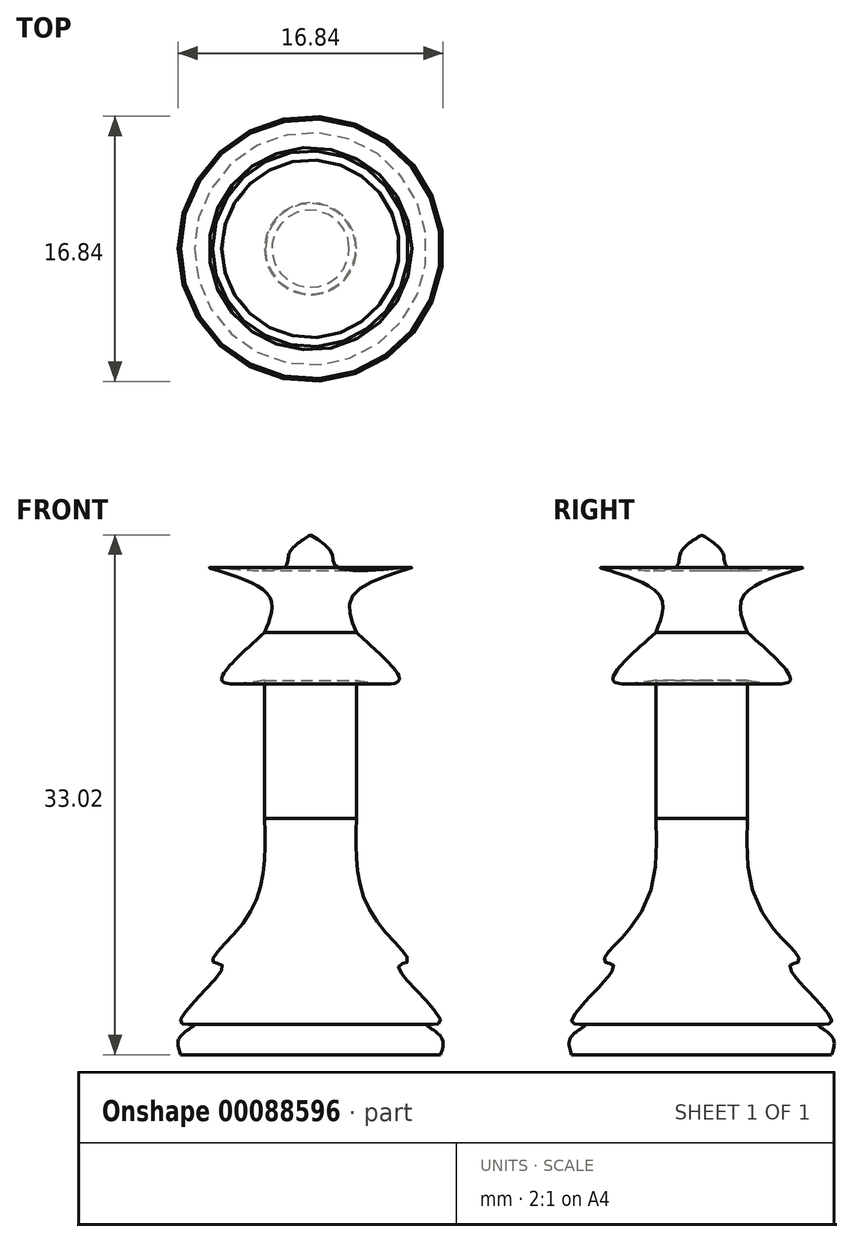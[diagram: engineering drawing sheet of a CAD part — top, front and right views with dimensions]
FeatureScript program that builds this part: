
annotation { "Feature Type Name" : "Feature", "Feature Type Description" : "" }
export const myFeature = defineFeature(function(context is Context, id is Id, definition is map)
    precondition{}
    {
        {
            var Q0;
            Q0=qCreatedBy(makeId("Front.planeOp"),FACE);
            var sketch = newSketch(context, id + "F0", { "sketchPlane" : qUnion([Q0])});
            skLineSegment(sketch, "E0", {"start": v(0, 0) * mm, "end": v(0, 33.02) * mm});
            skLineSegment(sketch, "E1", {"start": v(0, 0) * mm, "end": v(8.26, 0) * mm});
            skFitSpline(sketch, "E2", {"points": [v(8.26, 0) * mm, v(8.26, 1.17) * mm, v(7.4, 1.9) * mm, v(8.26, 2.07) * mm, v(5.59, 5.6) * mm, v(6.2, 5.91) * mm, v(3.94, 8.86) * mm, v(2.92, 15) * mm], "startDerivative": vector(4.08, 11.76) * mm, "endDerivative": vector(0.89, 27.02) * mm});
            skFitSpline(sketch, "E3", {"points": [v(2.92, 15) * mm, v(2.92, 23.77) * mm], "startDerivative": vector(0, 8.76) * mm, "endDerivative": vector(0, 8.76) * mm});
            skFitSpline(sketch, "E4", {"points": [v(2.92, 23.77) * mm, v(5.62, 23.77) * mm, v(2.92, 26.8) * mm], "startDerivative": vector(8.49, -1.24) * mm, "endDerivative": vector(-7.93, 7.03) * mm});
            skFitSpline(sketch, "E5", {"points": [v(2.92, 26.8) * mm, v(2.92, 29.45) * mm, v(6.43, 30.95) * mm, v(1.77, 30.9) * mm, v(1.37, 31.8) * mm, v(0, 33.02) * mm], "startDerivative": vector(-5.95, 14.27) * mm, "endDerivative": vector(-10.93, 6.85) * mm});
            skSolve(sketch);
        }
        {
            var Q0;
            Q0=qCreatedBy(makeId("Front.planeOp"),FACE);
            var sketch = newSketch(context, id + "F1", { "sketchPlane" : qUnion([Q0])});
            skLineSegment(sketch, "E6", {"start": v(0, 0) * mm, "end": v(0, 33.32) * mm});
            skSolve(sketch);
        }
        {
            var Q0;
            Q0=makeQuery(id+"F0.imprint","IMPRINT",FACE,{"disambiguationData":[TD([[makeQuery(id+"F0.imprint","IMPRINT",EDGE,{"derivedFrom":sQuery(id+"F0.wireOp",EDGE,"E0")}),-1.0]])]});
            var Q1;
            Q1=sQuery(id+"F1.wireOp",EDGE,"E6");
            revolve(context, id + "F2", {"entities" : qUnion([Q0]), "axis" : qUnion([Q1]), "revolveType" : RevolveType.FULL});
        }
    });
